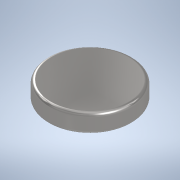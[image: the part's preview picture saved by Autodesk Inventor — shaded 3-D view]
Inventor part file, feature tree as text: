
AUTODESK INVENTOR PART (.ipt)
format: ipt  version: 2020 (Build 240168000, 168)  size: 160,256 bytes
history: native  units: mm
features: extrude x1, fillet x1
ambient origin geometry x8: Origin, YZ Plane, XZ Plane, XY Plane, X Axis, Y Axis, Z Axis, Center Point
bodies: Volumenkörper1 (feature_tree)
feature tree (2):
  extrude  "Extrusion1"  Depth=12.0mm
  fillet  "Rundung1"  Radius=2.6mm
